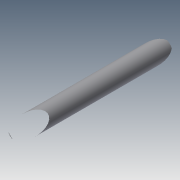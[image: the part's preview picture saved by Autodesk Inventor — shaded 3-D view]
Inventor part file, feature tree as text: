
AUTODESK INVENTOR PART (.ipt)
format: ipt  version: 2015 (Build 190159000, 159)  size: 70,656 bytes
history: native  units: mm
features: extrude x1, sketch x1
ambient origin geometry x8: Origin, YZ Plane, XZ Plane, XY Plane, X Axis, Y Axis, Z Axis, Center Point
bodies: Solid1 (feature_tree)
feature tree (2):
  extrude  "Extrusion1"  Depth=80.0mm TaperAngle=0.0deg
  sketch  "Sketch1"  dims[d0=10.0mm d1=80.0mm d2=0.0mm]
